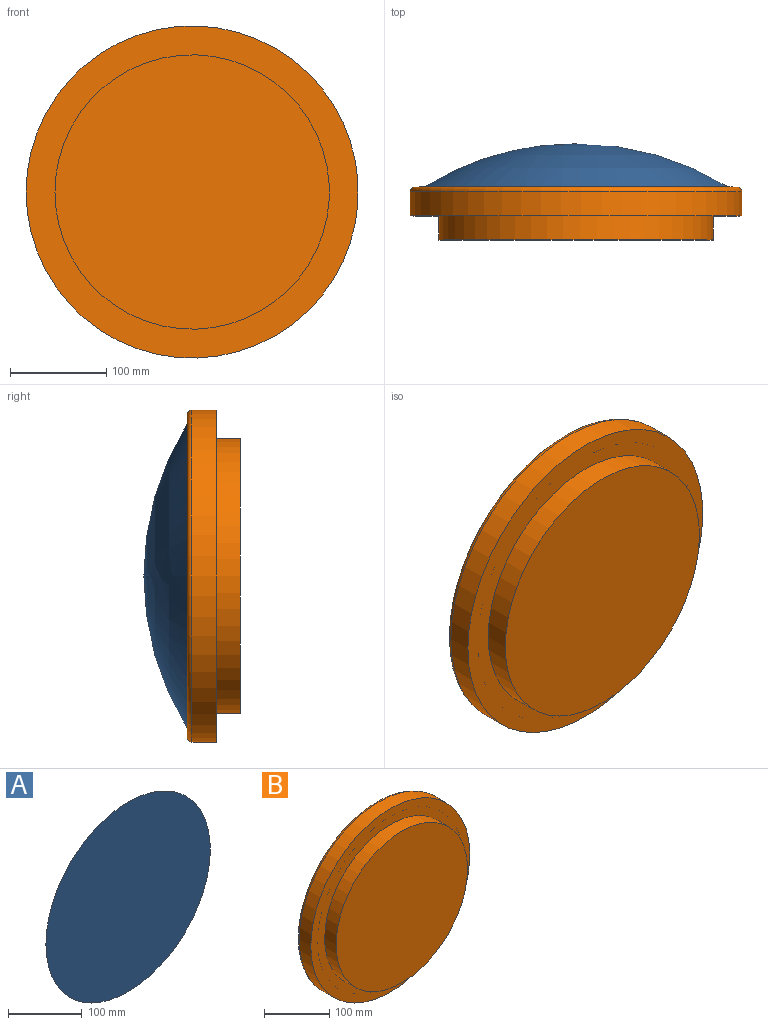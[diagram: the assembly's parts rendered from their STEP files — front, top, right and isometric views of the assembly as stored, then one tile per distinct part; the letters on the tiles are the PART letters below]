
ASSEMBLY  parts=2 mates=1
PART A: 2 faces, bbox 316.1x45x316.1 mm
  f0: plane 316.07x316.07mm, normal (0,-1,0), area 78461.3mm2, adj f1
  f1: sphere r=300mm, area 84823mm2, adj f0
PART B: 8 faces, bbox 373.4x55x373.4 mm
  f0: cylinder r=142.5mm len=285mm, axis (0,-1,0), area 22383.8mm2, adj f1,f5
  f1: plane 285x285mm, normal (0,-1,0), area 63794mm2, adj f0
  f2: cylinder r=157.5mm len=315mm, axis (0,-1,0), area 28698.4mm2, adj f3,f6
  f3: plane 315x315mm, normal (0,1,0), area 77931.1mm2, adj f2
  f4: cylinder r=172.5mm len=345mm, axis (0,-1,0), area 27096.2mm2, adj f5,f7
  f5: plane 345x345mm, normal (0,-1,0), area 29688.1mm2, adj f0,f4
  f6: plane 335x335mm, normal (0,1,0), area 10210.2mm2, adj f2,f7
  f7: torus R=167.5mm, axis (0,1,0), area 8422.9mm2, adj f4,f6
PLACE A t=(-8511.64,72.92,-15000)mm
PLACE B t=(-8511.64,72.92,-15000)mm
MATE fastened A.f0 <-> B.f7  axis (0,-1,0) through (0,55,0)mm
